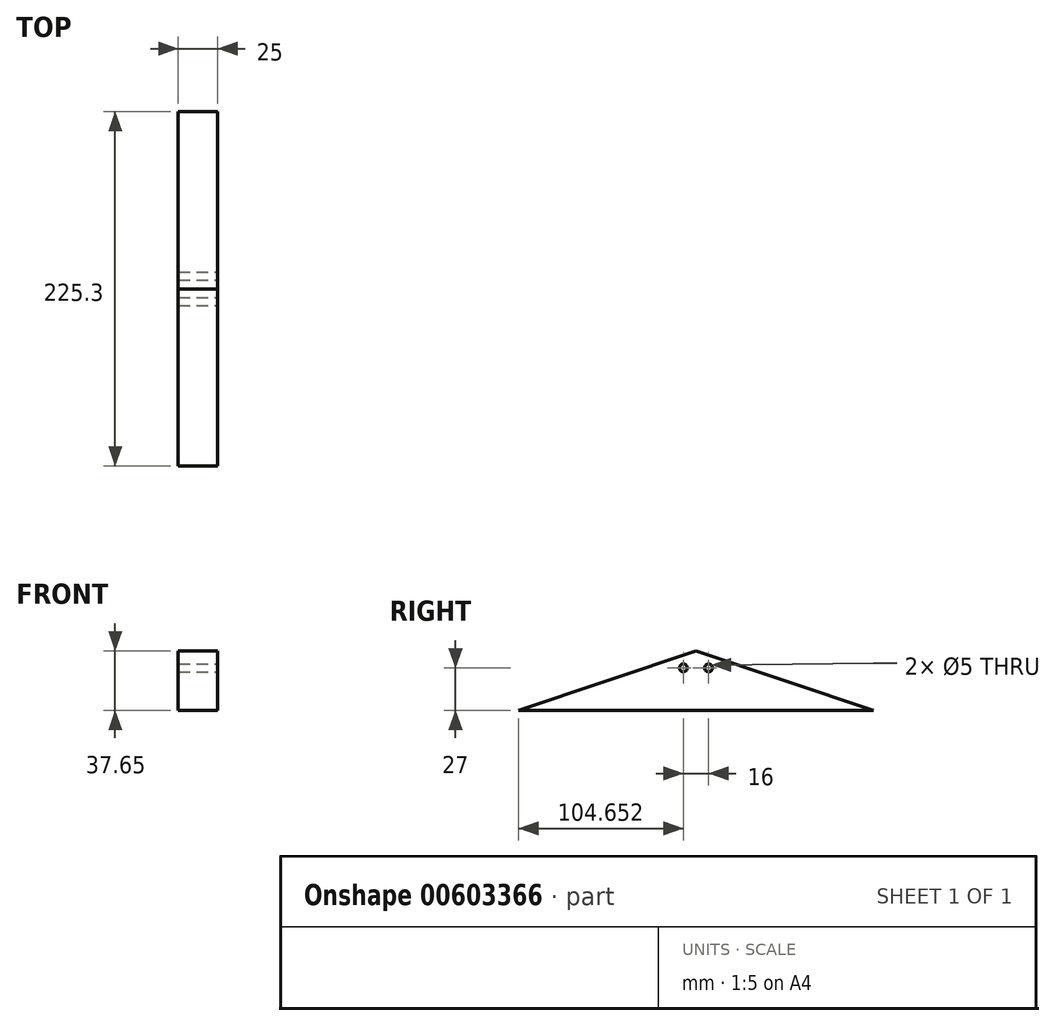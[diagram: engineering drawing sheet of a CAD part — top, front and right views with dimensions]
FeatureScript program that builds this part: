
annotation { "Feature Type Name" : "Feature", "Feature Type Description" : "" }
export const myFeature = defineFeature(function(context is Context, id is Id, definition is map)
    precondition{}
    {
        {
            var Q0;
            Q0=qCreatedBy(makeId("Top.planeOp"),FACE);
            var sketch = newSketch(context, id + "F0", { "sketchPlane" : qUnion([Q0])});
            skLineSegment(sketch, "E0", {"start": v(-327.3, -140.86) * mm, "end": v(-102.6, -140.86) * mm});
            skLineSegment(sketch, "E1", {"start": v(-102.6, -140.86) * mm, "end": v(-102.6, -170.86) * mm});
            skLineSegment(sketch, "E2", {"start": v(-102.6, -170.86) * mm, "end": v(0, -170.86) * mm});
            skLineSegment(sketch, "E3", {"start": v(0, -170.86) * mm, "end": v(0, -140.86) * mm});
            skLineSegment(sketch, "E4", {"start": v(0, -140.86) * mm, "end": v(288.9, -140.86) * mm});
            skLineSegment(sketch, "E5", {"start": v(288.9, -140.86) * mm, "end": v(288.9, 108.14) * mm});
            skLineSegment(sketch, "E6", {"start": v(288.9, 108.14) * mm, "end": v(0, 108.14) * mm});
            skLineSegment(sketch, "E7", {"start": v(0, 108.14) * mm, "end": v(0, 138.14) * mm});
            skLineSegment(sketch, "E8", {"start": v(-102.6, 128.64) * mm, "end": v(-102.6, 108.14) * mm});
            skLineSegment(sketch, "E9", {"start": v(-102.6, 108.14) * mm, "end": v(-327.3, 108.14) * mm});
            skLineSegment(sketch, "E10", {"start": v(-327.3, 108.14) * mm, "end": v(-327.3, -140.86) * mm});
            skLineSegment(sketch, "E11", {"start": v(-102.6, 128.64) * mm, "end": v(0, 138.14) * mm});
            skSolve(sketch);
        }
        {
            var Q0;
            Q0=makeQuery(id+"F0.imprint","IMPRINT",FACE,{"disambiguationData":[TD([[makeQuery(id+"F0.imprint","IMPRINT",EDGE,{"derivedFrom":sQuery(id+"F0.wireOp",EDGE,"E0")}),1.0]])]});
            extrude(context, id + "F1", {"entities" : qUnion([Q0]), "depth" : 8 * mm, "offsetDistance" : 25 * mm});
        }
        {
            var Q0;
            Q0=makeQuery(id+"F1.opExtrude","SWEPT_FACE",FACE,{"disambiguationData":[OSD([sQuery(id+"F0.wireOp",EDGE,"E5")])]});
            var sketch = newSketch(context, id + "F2", { "sketchPlane" : qUnion([Q0])});
            skLineSegment(sketch, "E12", {"start": v(-146.36, 8) * mm, "end": v(113.64, 8) * mm});
            skPoint(sketch, "E13", {"position": v(-140.86, 8) * mm});
            skPoint(sketch, "E14", {"position": v(108.14, 8) * mm});
            skLineSegment(sketch, "E15", {"start": v(-146.36, 8) * mm, "end": v(-16.36, 51.45) * mm});
            skLineSegment(sketch, "E16", {"start": v(-16.36, 51.45) * mm, "end": v(113.64, 8) * mm});
            skPoint(sketch, "E17", {"position": v(-16.36, 8) * mm});
            skSolve(sketch);
        }
        {
            var Q0;
            {var subQ0=sQuery(id+"F2.wireOp",EDGE,"E15");Q0=makeQuery(id+"F2.imprint","IMPRINT",FACE,{"disambiguationData":[TD([[makeQuery(id+"F2.imprint","IMPRINT",EDGE,{"derivedFrom":subQ0}),-1.0]])]});}
            extrude(context, id + "F3", {"entities" : qUnion([Q0]), "operationType" : NewBodyOperationType.ADD, "oppositeDirection" : true, "depth" : (616.2 + 5.5) * mm, "offsetDistance" : 25 * mm});
        }
        {
            var Q0;
            Q0=qSketchRegion(id+"F2",true);
            extrude(context, id + "F4", {"entities" : qUnion([Q0]), "operationType" : NewBodyOperationType.ADD, "depth" : 5.5 * mm, "offsetDistance" : 25 * mm});
        }
        {
            var Q0;
            Q0=makeQuery(id+"F1.opExtrude","SWEPT_FACE",FACE,{"disambiguationData":[OSD([sQuery(id+"F0.wireOp",EDGE,"E2")])]});
            var sketch = newSketch(context, id + "F5", { "sketchPlane" : qUnion([Q0])});
            skLineSegment(sketch, "E18", {"start": v(-108.1, 8) * mm, "end": v(5.5, 8) * mm});
            skPoint(sketch, "E19", {"position": v(-102.6, 8) * mm});
            skPoint(sketch, "E20", {"position": v(0, 8) * mm});
            skPoint(sketch, "E21", {"position": v(-51.3, 8) * mm});
            skLineSegment(sketch, "E22", {"start": v(-51.3, 8) * mm, "end": v(-51.3, 90.85) * mm, "construction": true});
            skPoint(sketch, "E23", {"position": v(-51.3, 62.75) * mm});
            skLineSegment(sketch, "E24", {"start": v(-108.1, 8) * mm, "end": v(-51.3, 62.75) * mm});
            skLineSegment(sketch, "E25", {"start": v(-51.3, 62.75) * mm, "end": v(5.5, 8) * mm});
            skSolve(sketch);
        }
        {
            var Q0;
            Q0=qSketchRegion(id+"F5",true);
            var Q1;
            Q1=makeQuery(id+"F1.opExtrude","SWEPT_FACE",FACE,{"disambiguationData":[OSD([sQuery(id+"F0.wireOp",EDGE,"E11")])]});
            extrude(context, id + "F6", {"entities" : qUnion([Q0]), "operationType" : NewBodyOperationType.ADD, "endBound" : BoundingType.UP_TO_SURFACE, "oppositeDirection" : true, "depth" : 25 * mm, "endBoundEntityFace" : qUnion([Q1]), "hasOffset" : true, "offsetDistance" : -5.5 * mm});
        }
        {
            var Q0;
            Q0=qSketchRegion(id+"F5",true);
            extrude(context, id + "F7", {"entities" : qUnion([Q0]), "operationType" : NewBodyOperationType.ADD, "depth" : 5.5 * mm, "offsetDistance" : 25 * mm});
        }
        {
            var Q0;
            Q0=makeQuery(id+"F6.opExtrude","CAP_FACE",FACE,{"disambiguationData":[OSD([sQuery(id+"F5.wireOp",EDGE,"E18"),sQuery(id+"F5.wireOp",EDGE,"E24"),sQuery(id+"F5.wireOp",EDGE,"E25")])],"isStart":false});
            var sketch = newSketch(context, id + "F8", { "sketchPlane" : qUnion([Q0])});
            skLineSegment(sketch, "E26.0", {"start": v(38.28, 55.82) * mm, "end": v(-15.3, 4.4) * mm});
            skLineSegment(sketch, "E26.1", {"start": v(91.86, 4.4) * mm, "end": v(38.28, 55.82) * mm});
            skLineSegment(sketch, "E27", {"start": v(-15.3, 4.4) * mm, "end": v(91.86, 4.4) * mm});
            skSolve(sketch);
        }
        {
            var Q0;
            {var subQ0=sQuery(id+"F8.wireOp",EDGE,"E26.1");var subQ1=sQuery(id+"F8.wireOp",EDGE,"E26.0");var subQ2=makeQuery(id+"F8.imprint","INTERSECT",VERTEX,{"derivedFrom":[subQ1,subQ0]});Q0=makeQuery(id+"F8.imprint","IMPRINT",FACE,{"disambiguationData":[TD([[makeQuery(id+"F8.imprint","IMPRINT",EDGE,{"disambiguationData":[TD([[subQ2,-1.0]])],"derivedFrom":subQ1}),1.0]])]});}
            extrude(context, id + "F9", {"entities" : qUnion([Q0]), "operationType" : NewBodyOperationType.REMOVE, "oppositeDirection" : true, "depth" : 5.5 * mm, "offsetDistance" : 25 * mm});
        }
        {
            var Q0;
            Q0=makeQuery(id+"F3.opExtrude","CAP_FACE",FACE,{"disambiguationData":[OSD([sQuery(id+"F2.wireOp",EDGE,"E12"),sQuery(id+"F2.wireOp",EDGE,"E15"),sQuery(id+"F2.wireOp",EDGE,"E16")])],"isStart":false});
            var sketch = newSketch(context, id + "F10", { "sketchPlane" : qUnion([Q0])});
            skLineSegment(sketch, "E28.0", {"start": v(16.36, 45.65) * mm, "end": v(-111.9, 2.78) * mm});
            skLineSegment(sketch, "E28.1", {"start": v(144.61, 2.78) * mm, "end": v(16.36, 45.65) * mm});
            skLineSegment(sketch, "E29", {"start": v(-111.9, 2.78) * mm, "end": v(144.61, 2.78) * mm});
            skSolve(sketch);
        }
        {
            var Q0;
            Q0=qSketchRegion(id+"F10",true);
            extrude(context, id + "F11", {"entities" : qUnion([Q0]), "operationType" : NewBodyOperationType.REMOVE, "oppositeDirection" : true, "depth" : 5.5 * mm, "offsetDistance" : 25 * mm});
        }
        {
            var Q0;
            Q0=makeQuery(id+"F4.opExtrude","CAP_FACE",FACE,{"disambiguationData":[OSD([sQuery(id+"F2.wireOp",EDGE,"E12"),sQuery(id+"F2.wireOp",EDGE,"E15"),sQuery(id+"F2.wireOp",EDGE,"E16")])],"isStart":false});
            var sketch = newSketch(context, id + "F12", { "sketchPlane" : qUnion([Q0])});
            skLineSegment(sketch, "E30.0", {"start": v(-16.36, 45.65) * mm, "end": v(111.9, 2.78) * mm});
            skLineSegment(sketch, "E30.1", {"start": v(-144.61, 2.78) * mm, "end": v(-16.36, 45.65) * mm});
            skLineSegment(sketch, "E31", {"start": v(-144.61, 2.78) * mm, "end": v(111.9, 2.78) * mm});
            skSolve(sketch);
        }
        {
            var Q0;
            Q0=qSketchRegion(id+"F12",true);
            extrude(context, id + "F13", {"entities" : qUnion([Q0]), "operationType" : NewBodyOperationType.REMOVE, "oppositeDirection" : true, "depth" : 5.5 * mm, "offsetDistance" : 25 * mm});
        }
        {
            var Q0;
            Q0=makeQuery(id+"F7.opExtrude","CAP_FACE",FACE,{"disambiguationData":[OSD([sQuery(id+"F5.wireOp",EDGE,"E18"),sQuery(id+"F5.wireOp",EDGE,"E24"),sQuery(id+"F5.wireOp",EDGE,"E25")])],"isStart":false});
            var sketch = newSketch(context, id + "F14", { "sketchPlane" : qUnion([Q0])});
            skLineSegment(sketch, "E32.0", {"start": v(-51.3, 55.11) * mm, "end": v(1.68, 4.04) * mm});
            skLineSegment(sketch, "E32.1", {"start": v(-104.28, 4.04) * mm, "end": v(-51.3, 55.11) * mm});
            skLineSegment(sketch, "E33", {"start": v(-104.28, 4.04) * mm, "end": v(1.68, 4.04) * mm});
            skSolve(sketch);
        }
        {
            var Q0;
            Q0=qSketchRegion(id+"F14",true);
            extrude(context, id + "F15", {"entities" : qUnion([Q0]), "operationType" : NewBodyOperationType.REMOVE, "oppositeDirection" : true, "depth" : 5.5 * mm, "offsetDistance" : 25 * mm});
        }
        {
            var Q0;
            Q0=makeQuery(id+"F4.opExtrude","CAP_FACE",FACE,{"disambiguationData":[OSD([sQuery(id+"F2.wireOp",EDGE,"E12"),sQuery(id+"F2.wireOp",EDGE,"E15"),sQuery(id+"F2.wireOp",EDGE,"E16")])],"isStart":false});
            var sketch = newSketch(context, id + "F16", { "sketchPlane" : qUnion([Q0])});
            skLineSegment(sketch, "E34", {"start": v(-36.64, 44.67) * mm, "end": v(-16.36, 51.45) * mm});
            skLineSegment(sketch, "E35", {"start": v(-16.36, 51.45) * mm, "end": v(3.93, 44.67) * mm});
            skLineSegment(sketch, "E36.0", {"start": v(-16.36, 55.67) * mm, "end": v(5.2, 48.47) * mm});
            skLineSegment(sketch, "E36.1", {"start": v(-37.91, 48.47) * mm, "end": v(-16.36, 55.67) * mm});
            skLineSegment(sketch, "E37", {"start": v(-37.91, 48.47) * mm, "end": v(-36.64, 44.67) * mm});
            skLineSegment(sketch, "E38", {"start": v(5.2, 48.47) * mm, "end": v(3.93, 44.67) * mm});
            skSolve(sketch);
        }
        {
            var Q0;
            Q0=makeQuery(id+"F16.imprint","IMPRINT",FACE,{"disambiguationData":[TD([[makeQuery(id+"F16.imprint","IMPRINT",EDGE,{"derivedFrom":sQuery(id+"F16.wireOp",EDGE,"E34")}),1.0]])]});
            extrude(context, id + "F17", {"entities" : qUnion([Q0]), "operationType" : NewBodyOperationType.ADD, "oppositeDirection" : true, "depth" : (30.35 + 277.85) * mm, "offsetDistance" : 25 * mm});
        }
        {
            var Q0;
            Q0=qSketchRegion(id+"F16",true);
            extrude(context, id + "F18", {"entities" : qUnion([Q0]), "operationType" : NewBodyOperationType.REMOVE, "oppositeDirection" : true, "depth" : 24 * mm, "offsetDistance" : 25 * mm});
        }
        {
            var Q0;
            Q0=makeQuery(id+"F3.opExtrude","CAP_FACE",FACE,{"disambiguationData":[OSD([sQuery(id+"F2.wireOp",EDGE,"E12"),sQuery(id+"F2.wireOp",EDGE,"E15"),sQuery(id+"F2.wireOp",EDGE,"E16")])],"isStart":false});
            var sketch = newSketch(context, id + "F19", { "sketchPlane" : qUnion([Q0])});
            skLineSegment(sketch, "E39", {"start": v(-3.93, 44.67) * mm, "end": v(16.36, 51.45) * mm});
            skLineSegment(sketch, "E40", {"start": v(16.36, 51.45) * mm, "end": v(36.64, 44.67) * mm});
            skLineSegment(sketch, "E41.0", {"start": v(16.36, 55.67) * mm, "end": v(37.91, 48.47) * mm});
            skLineSegment(sketch, "E41.1", {"start": v(-5.2, 48.47) * mm, "end": v(16.36, 55.67) * mm});
            skLineSegment(sketch, "E42", {"start": v(-5.2, 48.47) * mm, "end": v(-3.93, 44.67) * mm});
            skLineSegment(sketch, "E43", {"start": v(37.91, 48.47) * mm, "end": v(36.64, 44.67) * mm});
            skSolve(sketch);
        }
        {
            var Q0;
            Q0=qSketchRegion(id+"F19",true);
            extrude(context, id + "F20", {"entities" : qUnion([Q0]), "operationType" : NewBodyOperationType.ADD, "oppositeDirection" : true, "depth" : (30.35 + 213.85) * mm, "offsetDistance" : 25 * mm});
        }
        {
            var Q0;
            Q0=qSketchRegion(id+"F19",true);
            extrude(context, id + "F21", {"entities" : qUnion([Q0]), "operationType" : NewBodyOperationType.REMOVE, "oppositeDirection" : true, "depth" : 30.35 * mm, "offsetDistance" : 25 * mm});
        }
        {
            var Q0;
            Q0=makeQuery(id+"F11.boolean.opBoolean","MERGE",FACE,{"derivedFrom":[makeQuery(id+"F1.opExtrude","SWEPT_FACE",FACE,{"disambiguationData":[OSD([sQuery(id+"F0.wireOp",EDGE,"E10")])]}),makeQuery(id+"F11.opExtrude","CAP_FACE",FACE,{"disambiguationData":[OSD([sQuery(id+"F10.wireOp",EDGE,"E28.0"),sQuery(id+"F10.wireOp",EDGE,"E28.1"),sQuery(id+"F10.wireOp",EDGE,"E29")])],"isStart":false})]});
            var sketch = newSketch(context, id + "F22", { "sketchPlane" : qUnion([Q0])});
            skPoint(sketch, "E44", {"position": v(16.36, 0) * mm});
            skLineSegment(sketch, "E45", {"start": v(16.36, 0) * mm, "end": v(16.36, 35) * mm, "construction": true});
            skLineSegment(sketch, "E46", {"start": v(-4.2, 35) * mm, "end": v(35.76, 35) * mm, "construction": true});
            skPoint(sketch, "E47", {"position": v(8.36, 35) * mm});
            skPoint(sketch, "E48", {"position": v(24.36, 35) * mm});
            skCircle(sketch, "E49", {"center": v(8.36, 35) * mm, "radius": 2.5 * mm});
            skCircle(sketch, "E50", {"center": v(24.36, 35) * mm, "radius": 2.5 * mm});
            skSolve(sketch);
        }
        {
            var Q0;
            Q0=qSketchRegion(id+"F22",true);
            extrude(context, id + "F23", {"entities" : qUnion([Q0]), "operationType" : NewBodyOperationType.REMOVE, "oppositeDirection" : true, "depth" : .5 * mm, "offsetDistance" : 25 * mm});
        }
        {
            var Q0;
            Q0=makeQuery(id+"F13.boolean.opBoolean","MERGE",FACE,{"derivedFrom":[makeQuery(id+"F3.boolean.opBoolean","MERGE",FACE,{"derivedFrom":[makeQuery(id+"F1.opExtrude","SWEPT_FACE",FACE,{"disambiguationData":[OSD([sQuery(id+"F0.wireOp",EDGE,"E5")])]}),makeQuery(id+"F3.opExtrude","CAP_FACE",FACE,{"disambiguationData":[OSD([sQuery(id+"F2.wireOp",EDGE,"E12"),sQuery(id+"F2.wireOp",EDGE,"E15"),sQuery(id+"F2.wireOp",EDGE,"E16")])],"isStart":true})]}),makeQuery(id+"F13.opExtrude","CAP_FACE",FACE,{"disambiguationData":[OSD([sQuery(id+"F12.wireOp",EDGE,"E30.0"),sQuery(id+"F12.wireOp",EDGE,"E30.1"),sQuery(id+"F12.wireOp",EDGE,"E31")])],"isStart":false})]});
            var sketch = newSketch(context, id + "F24", { "sketchPlane" : qUnion([Q0])});
            skPoint(sketch, "E51", {"position": v(-16.36, 0) * mm});
            skLineSegment(sketch, "E52", {"start": v(-16.36, 0) * mm, "end": v(-16.36, 35) * mm, "construction": true});
            skLineSegment(sketch, "E53", {"start": v(-48.45, 35) * mm, "end": v(-8.49, 35) * mm, "construction": true});
            skPoint(sketch, "E54", {"position": v(-24.36, 35) * mm});
            skPoint(sketch, "E55", {"position": v(-8.36, 35) * mm});
            skCircle(sketch, "E56", {"center": v(-24.36, 35) * mm, "radius": 2.5 * mm});
            skCircle(sketch, "E57", {"center": v(-8.36, 35) * mm, "radius": 2.5 * mm});
            skSolve(sketch);
        }
        {
            var Q0;
            Q0=qSketchRegion(id+"F24",true);
            extrude(context, id + "F25", {"entities" : qUnion([Q0]), "operationType" : NewBodyOperationType.REMOVE, "oppositeDirection" : true, "depth" : .5 * mm, "offsetDistance" : 25 * mm});
        }
        {
            var Q0;
            Q0=makeQuery(id+"F15.boolean.opBoolean","MERGE",FACE,{"derivedFrom":[makeQuery(id+"F6.boolean.opBoolean","MERGE",FACE,{"derivedFrom":[makeQuery(id+"F1.opExtrude","SWEPT_FACE",FACE,{"disambiguationData":[OSD([sQuery(id+"F0.wireOp",EDGE,"E2")])]}),makeQuery(id+"F6.opExtrude","CAP_FACE",FACE,{"disambiguationData":[OSD([sQuery(id+"F5.wireOp",EDGE,"E18"),sQuery(id+"F5.wireOp",EDGE,"E24"),sQuery(id+"F5.wireOp",EDGE,"E25")])],"isStart":true})]})],"fromTools":[makeQuery(id+"F15.opExtrude","CAP_FACE",FACE,{"disambiguationData":[OSD([sQuery(id+"F14.wireOp",EDGE,"E32.0"),sQuery(id+"F14.wireOp",EDGE,"E32.1"),sQuery(id+"F14.wireOp",EDGE,"E33")])],"isStart":false})]});
            var sketch = newSketch(context, id + "F26", { "sketchPlane" : qUnion([Q0])});
            skPoint(sketch, "E58", {"position": v(-51.3, 0) * mm});
            skLineSegment(sketch, "E59", {"start": v(-51.3, 0) * mm, "end": v(-51.3, 35) * mm, "construction": true});
            skLineSegment(sketch, "E60", {"start": v(-73.66, 35) * mm, "end": v(-33.7, 35) * mm, "construction": true});
            skPoint(sketch, "E61", {"position": v(-59.3, 35) * mm});
            skPoint(sketch, "E62", {"position": v(-43.3, 35) * mm});
            skCircle(sketch, "E63", {"center": v(-59.3, 35) * mm, "radius": 2.5 * mm});
            skCircle(sketch, "E64", {"center": v(-43.3, 35) * mm, "radius": 2.5 * mm});
            skSolve(sketch);
        }
        {
            var Q0;
            Q0=qSketchRegion(id+"F26",true);
            extrude(context, id + "F27", {"entities" : qUnion([Q0]), "operationType" : NewBodyOperationType.REMOVE, "oppositeDirection" : true, "depth" : .5 * mm, "offsetDistance" : 25 * mm});
        }
        {
            var Q0;
            Q0=makeQuery(id+"F1.opExtrude","SWEPT_FACE",FACE,{"disambiguationData":[OSD([sQuery(id+"F0.wireOp",EDGE,"E11")])]});
            var sketch = newSketch(context, id + "F28", { "sketchPlane" : qUnion([Q0])});
            skPoint(sketch, "E65", {"position": v(38.78, 0) * mm});
            skLineSegment(sketch, "E66", {"start": v(38.78, 0) * mm, "end": v(38.78, 35) * mm, "construction": true});
            skLineSegment(sketch, "E67", {"start": v(13.04, 35) * mm, "end": v(53, 35) * mm, "construction": true});
            skPoint(sketch, "E68", {"position": v(30.78, 35) * mm});
            skPoint(sketch, "E69", {"position": v(46.78, 35) * mm});
            skCircle(sketch, "E70", {"center": v(30.78, 35) * mm, "radius": 2.5 * mm});
            skCircle(sketch, "E71", {"center": v(46.78, 35) * mm, "radius": 2.5 * mm});
            skSolve(sketch);
        }
        {
            var Q0;
            Q0=qSketchRegion(id+"F28",true);
            extrude(context, id + "F29", {"entities" : qUnion([Q0]), "operationType" : NewBodyOperationType.REMOVE, "oppositeDirection" : true, "depth" : .5 * mm, "offsetDistance" : 25 * mm});
        }
        {
            var Q0;
            Q0=makeQuery(id+"F13.boolean.opBoolean","MERGE",FACE,{"derivedFrom":[makeQuery(id+"F3.boolean.opBoolean","MERGE",FACE,{"derivedFrom":[makeQuery(id+"F1.opExtrude","SWEPT_FACE",FACE,{"disambiguationData":[OSD([sQuery(id+"F0.wireOp",EDGE,"E5")])]}),makeQuery(id+"F3.opExtrude","CAP_FACE",FACE,{"disambiguationData":[OSD([sQuery(id+"F2.wireOp",EDGE,"E12"),sQuery(id+"F2.wireOp",EDGE,"E15"),sQuery(id+"F2.wireOp",EDGE,"E16")])],"isStart":true})]}),makeQuery(id+"F13.opExtrude","CAP_FACE",FACE,{"disambiguationData":[OSD([sQuery(id+"F12.wireOp",EDGE,"E30.0"),sQuery(id+"F12.wireOp",EDGE,"E30.1"),sQuery(id+"F12.wireOp",EDGE,"E31")])],"isStart":false})]});
            var sketch = newSketch(context, id + "F30", { "sketchPlane" : qUnion([Q0])});
            skPoint(sketch, "E72", {"position": v(-16.36, 0) * mm});
            skLineSegment(sketch, "E73", {"start": v(-16.36, 0) * mm, "end": v(-16.36, 40.85) * mm, "construction": true});
            skLineSegment(sketch, "E74.bottom", {"start": v(-23.43, 23) * mm, "end": v(-9.29, 23) * mm});
            skLineSegment(sketch, "E74.top", {"start": v(-23.43, 5) * mm, "end": v(-9.29, 5) * mm});
            skLineSegment(sketch, "E74.left", {"start": v(-23.43, 23) * mm, "end": v(-23.43, 5) * mm});
            skLineSegment(sketch, "E74.right", {"start": v(-9.29, 23) * mm, "end": v(-9.29, 5) * mm});
            skLineSegment(sketch, "E75.0", {"start": v(-21.5, 21.07) * mm, "end": v(-17.32, 21.07) * mm});
            skLineSegment(sketch, "E75.1", {"start": v(-21.5, 21.07) * mm, "end": v(-21.5, 14.96) * mm});
            skLineSegment(sketch, "E75.2", {"start": v(-21.5, 6.93) * mm, "end": v(-17.32, 6.93) * mm});
            skLineSegment(sketch, "E75.3", {"start": v(-11.21, 21.07) * mm, "end": v(-11.21, 14.96) * mm});
            skLineSegment(sketch, "E76.left", {"start": v(-17.32, 21.07) * mm, "end": v(-17.32, 14.96) * mm});
            skLineSegment(sketch, "E76.right", {"start": v(-15.4, 21.07) * mm, "end": v(-15.4, 14.96) * mm});
            skLineSegment(sketch, "E77.bottom", {"start": v(-11.21, 14.96) * mm, "end": v(-15.4, 14.96) * mm});
            skLineSegment(sketch, "E77.top", {"start": v(-11.21, 13.04) * mm, "end": v(-15.4, 13.04) * mm});
            skLineSegment(sketch, "E78.trimOffspring", {"start": v(-17.32, 14.96) * mm, "end": v(-21.5, 14.96) * mm});
            skLineSegment(sketch, "E79.trimOffspring", {"start": v(-17.32, 13.04) * mm, "end": v(-17.32, 6.93) * mm});
            skLineSegment(sketch, "E80.trimOffspring", {"start": v(-17.32, 13.04) * mm, "end": v(-21.5, 13.04) * mm});
            skLineSegment(sketch, "E81.trimOffspring", {"start": v(-15.4, 13.04) * mm, "end": v(-15.4, 6.93) * mm});
            skLineSegment(sketch, "E82.trimOffspring", {"start": v(-11.21, 13.04) * mm, "end": v(-11.21, 6.93) * mm});
            skLineSegment(sketch, "E83.trimOffspring", {"start": v(-21.5, 13.04) * mm, "end": v(-21.5, 6.93) * mm});
            skLineSegment(sketch, "E84.trimOffspring", {"start": v(-15.4, 21.07) * mm, "end": v(-11.21, 21.07) * mm});
            skLineSegment(sketch, "E85.trimOffspring", {"start": v(-15.4, 6.93) * mm, "end": v(-11.21, 6.93) * mm});
            skPoint(sketch, "E86", {"position": v(-16.36, 23) * mm});
            skLineSegment(sketch, "E87.1.0.0", {"start": v(19.6, 13.04) * mm, "end": v(19.6, 6.93) * mm});
            skPoint(sketch, "E87.1.0.1", {"position": v(18.64, 23) * mm});
            skLineSegment(sketch, "E87.1.0.2", {"start": v(19.6, 6.93) * mm, "end": v(23.79, 6.93) * mm});
            skLineSegment(sketch, "E87.1.0.3", {"start": v(13.5, 13.04) * mm, "end": v(13.5, 6.93) * mm});
            skLineSegment(sketch, "E87.1.0.4", {"start": v(17.68, 13.04) * mm, "end": v(17.68, 6.93) * mm});
            skLineSegment(sketch, "E87.1.0.5", {"start": v(11.57, 5) * mm, "end": v(25.71, 5) * mm});
            skLineSegment(sketch, "E87.1.0.6", {"start": v(11.57, 23) * mm, "end": v(25.71, 23) * mm});
            skLineSegment(sketch, "E87.1.0.7", {"start": v(25.71, 23) * mm, "end": v(25.71, 5) * mm});
            skLineSegment(sketch, "E87.1.0.8", {"start": v(11.57, 23) * mm, "end": v(11.57, 5) * mm});
            skLineSegment(sketch, "E87.1.0.9", {"start": v(23.79, 13.04) * mm, "end": v(23.79, 6.93) * mm});
            skLineSegment(sketch, "E87.1.0.10", {"start": v(23.79, 13.04) * mm, "end": v(19.6, 13.04) * mm});
            skLineSegment(sketch, "E87.1.0.11", {"start": v(17.68, 21.07) * mm, "end": v(17.68, 14.96) * mm});
            skLineSegment(sketch, "E87.1.0.12", {"start": v(13.5, 21.07) * mm, "end": v(17.68, 21.07) * mm});
            skLineSegment(sketch, "E87.1.0.13", {"start": v(19.6, 21.07) * mm, "end": v(19.6, 14.96) * mm});
            skLineSegment(sketch, "E87.1.0.14", {"start": v(13.5, 6.93) * mm, "end": v(17.68, 6.93) * mm});
            skLineSegment(sketch, "E87.1.0.15", {"start": v(23.79, 21.07) * mm, "end": v(23.79, 14.96) * mm});
            skLineSegment(sketch, "E87.1.0.16", {"start": v(17.68, 13.04) * mm, "end": v(13.5, 13.04) * mm});
            skLineSegment(sketch, "E87.1.0.17", {"start": v(17.68, 14.96) * mm, "end": v(13.5, 14.96) * mm});
            skLineSegment(sketch, "E87.1.0.18", {"start": v(23.79, 14.96) * mm, "end": v(19.6, 14.96) * mm});
            skLineSegment(sketch, "E87.1.0.19", {"start": v(19.6, 21.07) * mm, "end": v(23.79, 21.07) * mm});
            skLineSegment(sketch, "E87.1.0.20", {"start": v(13.5, 21.07) * mm, "end": v(13.5, 14.96) * mm});
            skLineSegment(sketch, "E87.direction1", {"start": v(-23.43, 5) * mm, "end": v(11.57, 5) * mm, "construction": true});
            skLineSegment(sketch, "E88.1.0.0", {"start": v(-50.4, 6.93) * mm, "end": v(-46.21, 6.93) * mm});
            skPoint(sketch, "E88.1.0.1", {"position": v(-51.36, 0) * mm});
            skLineSegment(sketch, "E88.1.0.2", {"start": v(-58.43, 5) * mm, "end": v(-44.29, 5) * mm});
            skLineSegment(sketch, "E88.1.0.3", {"start": v(-44.29, 23) * mm, "end": v(-44.29, 5) * mm});
            skLineSegment(sketch, "E88.1.0.4", {"start": v(-58.43, 23) * mm, "end": v(-58.43, 5) * mm});
            skLineSegment(sketch, "E88.1.0.5", {"start": v(-46.21, 21.07) * mm, "end": v(-46.21, 14.96) * mm});
            skLineSegment(sketch, "E88.1.0.6", {"start": v(-56.5, 6.93) * mm, "end": v(-52.32, 6.93) * mm});
            skPoint(sketch, "E88.1.0.7", {"position": v(-51.36, 23) * mm});
            skLineSegment(sketch, "E88.1.0.8", {"start": v(-50.4, 13.04) * mm, "end": v(-50.4, 6.93) * mm});
            skLineSegment(sketch, "E88.1.0.9", {"start": v(-52.32, 13.04) * mm, "end": v(-56.5, 13.04) * mm});
            skLineSegment(sketch, "E88.1.0.10", {"start": v(-52.32, 13.04) * mm, "end": v(-52.32, 6.93) * mm});
            skLineSegment(sketch, "E88.1.0.11", {"start": v(-58.43, 23) * mm, "end": v(-44.29, 23) * mm});
            skLineSegment(sketch, "E88.1.0.12", {"start": v(-52.32, 14.96) * mm, "end": v(-56.5, 14.96) * mm});
            skLineSegment(sketch, "E88.1.0.13", {"start": v(-46.21, 13.04) * mm, "end": v(-50.4, 13.04) * mm});
            skLineSegment(sketch, "E88.1.0.14", {"start": v(-46.21, 14.96) * mm, "end": v(-50.4, 14.96) * mm});
            skLineSegment(sketch, "E88.1.0.15", {"start": v(-50.4, 21.07) * mm, "end": v(-46.21, 21.07) * mm});
            skLineSegment(sketch, "E88.1.0.16", {"start": v(-56.5, 21.07) * mm, "end": v(-56.5, 14.96) * mm});
            skLineSegment(sketch, "E88.1.0.17", {"start": v(-56.5, 21.07) * mm, "end": v(-52.32, 21.07) * mm});
            skLineSegment(sketch, "E88.1.0.18", {"start": v(-50.4, 21.07) * mm, "end": v(-50.4, 14.96) * mm});
            skLineSegment(sketch, "E88.1.0.19", {"start": v(-52.32, 21.07) * mm, "end": v(-52.32, 14.96) * mm});
            skLineSegment(sketch, "E88.1.0.20", {"start": v(-56.5, 13.04) * mm, "end": v(-56.5, 6.93) * mm});
            skLineSegment(sketch, "E88.1.0.21", {"start": v(-46.21, 13.04) * mm, "end": v(-46.21, 6.93) * mm});
            skLineSegment(sketch, "E88.direction1", {"start": v(-23.43, 5) * mm, "end": v(-58.43, 5) * mm, "construction": true});
            skSolve(sketch);
        }
        {
            var Q0;
            Q0=qSketchRegion(id+"F30",true);
            extrude(context, id + "F31", {"entities" : qUnion([Q0]), "operationType" : NewBodyOperationType.REMOVE, "oppositeDirection" : true, "depth" : 0.5 * mm, "offsetDistance" : 25 * mm});
        }
        {
            var Q0;
            Q0=makeQuery(id+"F11.boolean.opBoolean","MERGE",FACE,{"derivedFrom":[makeQuery(id+"F1.opExtrude","SWEPT_FACE",FACE,{"disambiguationData":[OSD([sQuery(id+"F0.wireOp",EDGE,"E10")])]}),makeQuery(id+"F11.opExtrude","CAP_FACE",FACE,{"disambiguationData":[OSD([sQuery(id+"F10.wireOp",EDGE,"E28.0"),sQuery(id+"F10.wireOp",EDGE,"E28.1"),sQuery(id+"F10.wireOp",EDGE,"E29")])],"isStart":false})]});
            extrude(context, id + "F32", {"entities" : qUnion([Q0]), "depth" : 25 * mm, "offsetDistance" : 25 * mm});
        }
        {
            var Q0;
            Q0=makeQuery(id+"F1.opExtrude","SWEPT_BODY",BODY,{"disambiguationData":[OSD([sQuery(id+"F0.wireOp",EDGE,"E0"),sQuery(id+"F0.wireOp",EDGE,"E1"),sQuery(id+"F0.wireOp",EDGE,"E2"),sQuery(id+"F0.wireOp",EDGE,"E3"),sQuery(id+"F0.wireOp",EDGE,"E4"),sQuery(id+"F0.wireOp",EDGE,"E5"),sQuery(id+"F0.wireOp",EDGE,"E6"),sQuery(id+"F0.wireOp",EDGE,"E7"),sQuery(id+"F0.wireOp",EDGE,"E8"),sQuery(id+"F0.wireOp",EDGE,"E9"),sQuery(id+"F0.wireOp",EDGE,"E10"),sQuery(id+"F0.wireOp",EDGE,"E11")])]});
            deleteBodies(context, id + "F33", {"entities" : qUnion([Q0])});
        }
        {
            var Q0;
            {var subQ0=sQuery(id+"F0.wireOp",EDGE,"E10");Q0=makeQuery(id+"F32.opExtrude","SWEPT_FACE",FACE,{"disambiguationData":[OSD([subQ0]),TDD([makeQuery(id+"F1.opExtrude","CAP_EDGE",EDGE,{"disambiguationData":[OSD([subQ0])],"isStart":true})])]});}
            extrude(context, id + "F34", {"entities" : qUnion([Q0]), "operationType" : NewBodyOperationType.REMOVE, "oppositeDirection" : true, "depth" : 8 * mm, "offsetDistance" : 25 * mm});
        }
    });
